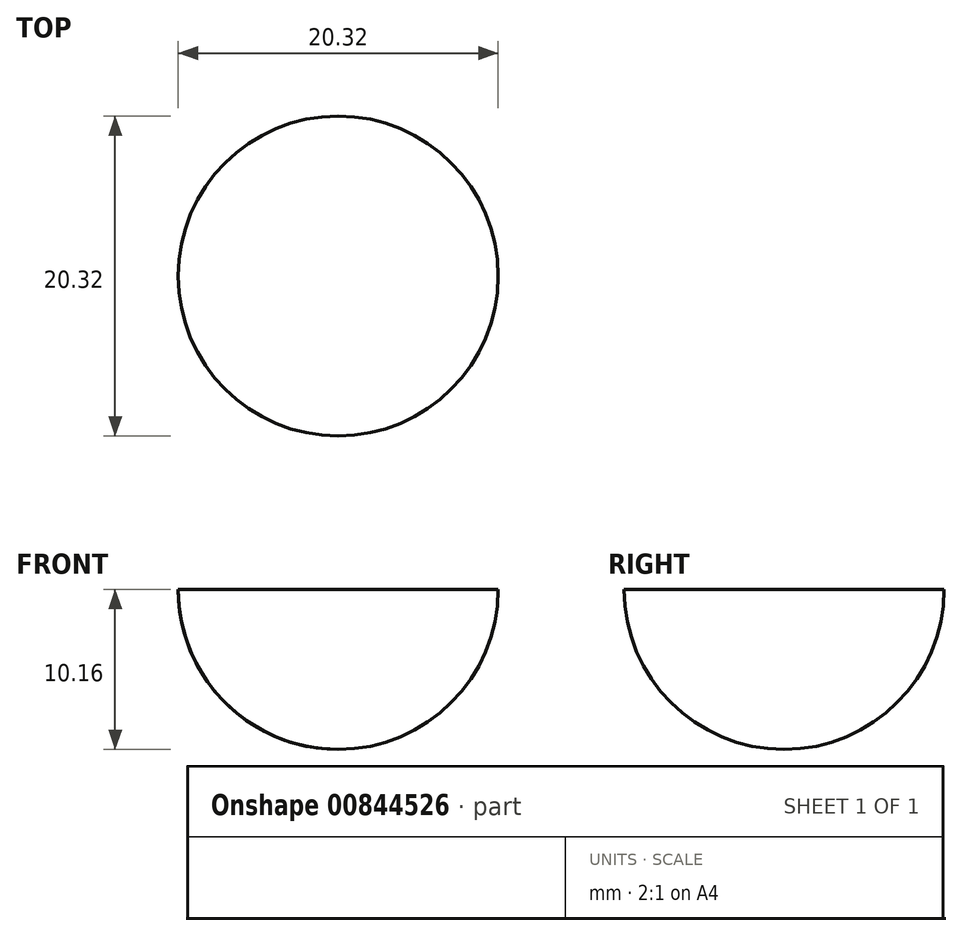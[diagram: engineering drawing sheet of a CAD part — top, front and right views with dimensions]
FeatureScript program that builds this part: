
annotation { "Feature Type Name" : "Feature", "Feature Type Description" : "" }
export const myFeature = defineFeature(function(context is Context, id is Id, definition is map)
    precondition{}
    {
        {
            var Q0;
            Q0=qCreatedBy(makeId("Front.planeOp"),FACE);
            var sketch = newSketch(context, id + "F0", { "sketchPlane" : qUnion([Q0])});
            skArc(sketch, "E0", {"start": v(0, -10.16) * mm, "mid": v(10.16, 0) * mm, "end": v(0, 10.16) * mm});
            skLineSegment(sketch, "E1", {"start": v(0, -10.16) * mm, "end": v(0, 10.16) * mm});
            skSolve(sketch);
        }
        {
            var Q0;
            Q0=qSketchRegion(id+"F0",true);
            var Q1;
            Q1=sQuery(id+"F0.wireOp",EDGE,"E1");
            revolve(context, id + "F1", {"surfaceOperationType" : NewSurfaceOperationType.NEW, "entities" : qUnion([Q0]), "axis" : qUnion([Q1]), "revolveType" : RevolveType.FULL});
        }
        {
            var Q0;
            Q0=qCreatedBy(makeId("Front.planeOp"),FACE);
            var sketch = newSketch(context, id + "F2", { "sketchPlane" : qUnion([Q0])});
            skLineSegment(sketch, "E2.bottom", {"start": v(-16.12, 0) * mm, "end": v(17.62, 0) * mm});
            skLineSegment(sketch, "E2.top", {"start": v(-16.12, 14.98) * mm, "end": v(17.62, 14.98) * mm});
            skLineSegment(sketch, "E2.left", {"start": v(-16.12, 0) * mm, "end": v(-16.12, 14.98) * mm});
            skLineSegment(sketch, "E2.right", {"start": v(17.62, 0) * mm, "end": v(17.62, 14.98) * mm});
            skSolve(sketch);
        }
        {
            var Q0;
            Q0=makeQuery(id+"F2.imprint","IMPRINT",FACE,{"disambiguationData":[TD([[makeQuery(id+"F2.imprint","IMPRINT",EDGE,{"derivedFrom":sQuery(id+"F2.wireOp",EDGE,"E2.bottom")}),1.0]])]});
            extrude(context, id + "F3", {"entities" : qUnion([Q0]), "operationType" : NewBodyOperationType.REMOVE, "endBound" : BoundingType.SYMMETRIC, "oppositeDirection" : true, "depth" : 25.4 * mm, "offsetDistance" : 25.4 * mm});
        }
    });
